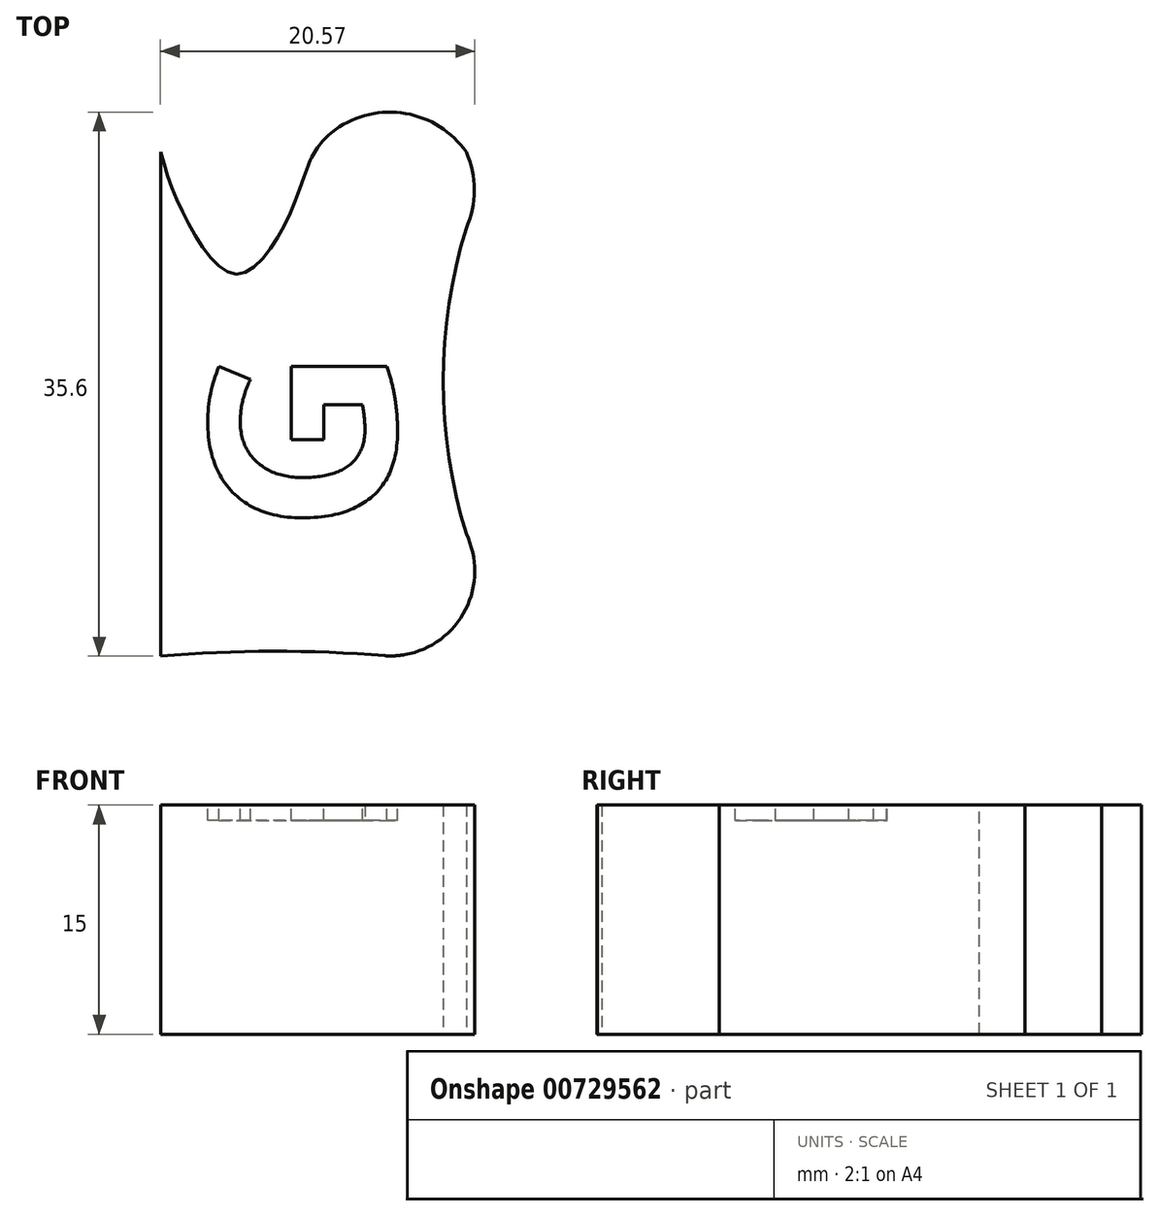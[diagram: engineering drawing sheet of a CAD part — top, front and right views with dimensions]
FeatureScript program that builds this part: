
annotation { "Feature Type Name" : "Feature", "Feature Type Description" : "" }
export const myFeature = defineFeature(function(context is Context, id is Id, definition is map)
    precondition{}
    {
        {
            var Q0;
            Q0=qCreatedBy(makeId("Top.planeOp"),FACE);
            var sketch = newSketch(context, id + "F0", { "sketchPlane" : qUnion([Q0])});
            skLineSegment(sketch, "E0", {"start": v(-17.97, 39.65) * mm, "end": v(-17.97, 6.65) * mm});
            skLineSegment(sketch, "E1", {"start": v(-17.97, 39.65) * mm, "end": v(-7.97, 39.65) * mm, "construction": true});
            skLineSegment(sketch, "E2", {"start": v(-17.97, 6.65) * mm, "end": v(-2.97, 6.65) * mm, "construction": true});
            skLineSegment(sketch, "E3", {"start": v(-17.97, 14.65) * mm, "end": v(2.03, 14.65) * mm, "construction": true});
            skLineSegment(sketch, "E4", {"start": v(-17.97, 34.65) * mm, "end": v(2.03, 34.65) * mm, "construction": true});
            skLineSegment(sketch, "E5", {"start": v(-17.97, 31.65) * mm, "end": v(-12.97, 31.65) * mm, "construction": true});
            skLineSegment(sketch, "E6", {"start": v(0.53, 24.65) * mm, "end": v(-17.97, 24.65) * mm, "construction": true});
            skLineSegment(sketch, "E7", {"start": v(-2.97, 42.25) * mm, "end": v(-17.97, 42.25) * mm, "construction": true});
            skLineSegment(sketch, "E8", {"start": v(-7.97, 39.65) * mm, "end": v(2.03, 39.65) * mm, "construction": true});
            skArc(sketch, "E9", {"start": v(2.03, 39.65) * mm, "mid": v(-1.93, 42.16) * mm, "end": v(-6.51, 41.11) * mm});
            skArc(sketch, "E10", {"start": v(2.03, 34.65) * mm, "mid": v(2.57, 37.15) * mm, "end": v(2.03, 39.65) * mm});
            skArc(sketch, "E11", {"start": v(2.03, 34.65) * mm, "mid": v(0.53, 24.65) * mm, "end": v(2.03, 14.65) * mm});
            skArc(sketch, "E12", {"start": v(-1.98, 6.74) * mm, "mid": v(2, 9.7) * mm, "end": v(2.03, 14.65) * mm});
            skArc(sketch, "E13", {"start": v(-3.27, 6.67) * mm, "mid": v(-10.62, 6.96) * mm, "end": v(-17.97, 6.65) * mm});
            skPoint(sketch, "E14", {"position": v(-15.97, 34.65) * mm});
            skPoint(sketch, "E15", {"position": v(-9.97, 34.65) * mm});
            skFitSpline(sketch, "E16", {"points": [v(-17.97, 39.65) * mm, v(-15.97, 34.65) * mm, v(-12.97, 31.65) * mm, v(-9.97, 34.65) * mm, v(-7.97, 39.65) * mm], "startDerivative": vector(5.02, -18.93) * mm, "endDerivative": vector(7.48, 18.68) * mm});
            skArc(sketch, "E17.filletArc", {"start": v(-6.51, 41.11) * mm, "mid": v(-7.58, 40.08) * mm, "end": v(-8.3, 38.77) * mm});
            skPoint(sketch, "E18.visualSharp", {"position": v(-2.97, 6.65) * mm});
            skArc(sketch, "E18.filletArc", {"start": v(-3.27, 6.67) * mm, "mid": v(-2.62, 6.66) * mm, "end": v(-1.98, 6.74) * mm});
            skSolve(sketch);
        }
        {
            var Q0;
            Q0 = qSketchRegion(id + "F0", true);
            extrude(context, id + "F1", {"entities" : qUnion([Q0]), "depth" : 15 * mm, "offsetDistance" : 25 * mm});
        }
        {
            var Q0;
            Q0=makeQuery(id+"F1.opExtrude","CAP_FACE",FACE,{"disambiguationData":[OSD([sQuery(id+"F0.wireOp",EDGE,"E0"),sQuery(id+"F0.wireOp",EDGE,"E9"),sQuery(id+"F0.wireOp",EDGE,"E10"),sQuery(id+"F0.wireOp",EDGE,"E11"),sQuery(id+"F0.wireOp",EDGE,"E12"),sQuery(id+"F0.wireOp",EDGE,"E13"),sQuery(id+"F0.wireOp",EDGE,"E16"),sQuery(id+"F0.wireOp",EDGE,"E17.filletArc"),sQuery(id+"F0.wireOp",EDGE,"E18.filletArc")])],"isStart":false});
            var sketch = newSketch(context, id + "F2", { "sketchPlane" : qUnion([Q0])});
            skText(sketch, "E19", { "text": "G", "fontName": "OpenSans-Bold.ttf"});
            skLineSegment(sketch, "E20", {"start": v(-14.72, 20.71) * mm, "end": v(-17.97, 20.71) * mm, "construction": true});
            skPoint(sketch, "E20.endSnap0", {"position": v(-17.97, 23.15) * mm});
            skPoint(sketch, "E20.endSnap1", {"position": v(-14.72, 20.71) * mm});
            skLineSegment(sketch, "E21", {"start": v(0.53, 24.65) * mm, "end": v(-2.72, 24.65) * mm, "construction": true});
            skLineSegment(sketch, "E22", {"start": v(-2.72, 26.8) * mm, "end": v(-14.72, 14.62) * mm, "construction": true});
            skPoint(sketch, "E23", {"position": v(-8.72, 20.71) * mm});
            const initialGuessF2  = {"E19": [-0.01472, 0.01462, 1, 0, 0.01219]};
            skSetInitialGuess(sketch, initialGuessF2);
            skSolve(sketch);
        }
        {
            var Q0;
            Q0=makeQuery(id+"F2.imprint","IMPRINT",FACE,{"disambiguationData":[TD([[makeQuery(id+"F2.imprint","IMPRINT",EDGE,{"derivedFrom":sQuery(id+"F2.wireOp",EDGE,"E19.sketch_text.stroke-0")}),-1.0]])]});
            extrude(context, id + "F3", {"entities" : qUnion([Q0]), "oppositeDirection" : true, "depth" : 1 * mm, "offsetDistance" : 25 * mm});
        }
        {
            var Q0;
            Q0=qCreatedBy(makeId("Right.planeOp"),FACE);
            var Q1;
            Q1=sQuery(id+"F2.wireOp",VERTEX,"E23");
            cPlane(context, id + "F4", {"entities" : qUnion([Q0, Q1]), "cplaneType" : CPlaneType.PLANE_POINT, "offset" : 25 * mm, "width" : 150 * mm, "height" : 150 * mm});
        }
        {
            var Q0;
            Q0=qCreatedBy(id+"F4.planeOp",FACE);
            var sketch = newSketch(context, id + "F5", { "sketchPlane" : qUnion([Q0])});
            skLineSegment(sketch, "E24", {"start": v(20.71, 15) * mm, "end": v(20.71, 2.07) * mm});
            skSolve(sketch);
        }
        {
            var Q0;
            Q0=makeQuery(id+"F3.opExtrude","SWEPT_BODY",BODY,{"disambiguationData":[OSD([sQuery(id+"F2.wireOp",EDGE,"E19.sketch_text.stroke-0"),sQuery(id+"F2.wireOp",EDGE,"E19.sketch_text.stroke-1"),sQuery(id+"F2.wireOp",EDGE,"E19.sketch_text.stroke-2"),sQuery(id+"F2.wireOp",EDGE,"E19.sketch_text.stroke-3"),sQuery(id+"F2.wireOp",EDGE,"E19.sketch_text.stroke-4"),sQuery(id+"F2.wireOp",EDGE,"E19.sketch_text.stroke-5"),sQuery(id+"F2.wireOp",EDGE,"E19.sketch_text.stroke-6"),sQuery(id+"F2.wireOp",EDGE,"E19.sketch_text.stroke-7"),sQuery(id+"F2.wireOp",EDGE,"E19.sketch_text.stroke-8"),sQuery(id+"F2.wireOp",EDGE,"E19.sketch_text.stroke-9"),sQuery(id+"F2.wireOp",EDGE,"E19.sketch_text.stroke-10"),sQuery(id+"F2.wireOp",EDGE,"E19.sketch_text.stroke-11"),sQuery(id+"F2.wireOp",EDGE,"E19.sketch_text.stroke-12"),sQuery(id+"F2.wireOp",EDGE,"E19.sketch_text.stroke-13"),sQuery(id+"F2.wireOp",EDGE,"E19.sketch_text.stroke-14"),sQuery(id+"F2.wireOp",EDGE,"E19.sketch_text.stroke-15"),sQuery(id+"F2.wireOp",EDGE,"E19.sketch_text.stroke-16"),sQuery(id+"F2.wireOp",EDGE,"E19.sketch_text.stroke-17"),sQuery(id+"F2.wireOp",EDGE,"E19.sketch_text.stroke-18")])]});
            var Q1;
            Q1=sQuery(id+"F5.wireOp",EDGE,"E24");
            transform(context, id + "F6", {"entities" : qUnion([Q0]), "transformType" : TransformType.ROTATION, "transformAxis" : qUnion([Q1]), "angle" : 270 * degree, "makeCopy" : false});
        }
        {
            var Q0;
            Q0=makeQuery(id+"F3.opExtrude","SWEPT_BODY",BODY,{"disambiguationData":[OSD([sQuery(id+"F2.wireOp",EDGE,"E19.sketch_text.stroke-0"),sQuery(id+"F2.wireOp",EDGE,"E19.sketch_text.stroke-1"),sQuery(id+"F2.wireOp",EDGE,"E19.sketch_text.stroke-2"),sQuery(id+"F2.wireOp",EDGE,"E19.sketch_text.stroke-3"),sQuery(id+"F2.wireOp",EDGE,"E19.sketch_text.stroke-4"),sQuery(id+"F2.wireOp",EDGE,"E19.sketch_text.stroke-5"),sQuery(id+"F2.wireOp",EDGE,"E19.sketch_text.stroke-6"),sQuery(id+"F2.wireOp",EDGE,"E19.sketch_text.stroke-7"),sQuery(id+"F2.wireOp",EDGE,"E19.sketch_text.stroke-8"),sQuery(id+"F2.wireOp",EDGE,"E19.sketch_text.stroke-9"),sQuery(id+"F2.wireOp",EDGE,"E19.sketch_text.stroke-10"),sQuery(id+"F2.wireOp",EDGE,"E19.sketch_text.stroke-11"),sQuery(id+"F2.wireOp",EDGE,"E19.sketch_text.stroke-12"),sQuery(id+"F2.wireOp",EDGE,"E19.sketch_text.stroke-13"),sQuery(id+"F2.wireOp",EDGE,"E19.sketch_text.stroke-14"),sQuery(id+"F2.wireOp",EDGE,"E19.sketch_text.stroke-15"),sQuery(id+"F2.wireOp",EDGE,"E19.sketch_text.stroke-16"),sQuery(id+"F2.wireOp",EDGE,"E19.sketch_text.stroke-17"),sQuery(id+"F2.wireOp",EDGE,"E19.sketch_text.stroke-18")])]});
            var Q1;
            Q1=makeQuery(id+"F1.opExtrude","SWEPT_BODY",BODY,{"disambiguationData":[OSD([sQuery(id+"F0.wireOp",EDGE,"E0"),sQuery(id+"F0.wireOp",EDGE,"E9"),sQuery(id+"F0.wireOp",EDGE,"E10"),sQuery(id+"F0.wireOp",EDGE,"E11"),sQuery(id+"F0.wireOp",EDGE,"E12"),sQuery(id+"F0.wireOp",EDGE,"E13"),sQuery(id+"F0.wireOp",EDGE,"E16"),sQuery(id+"F0.wireOp",EDGE,"E17.filletArc"),sQuery(id+"F0.wireOp",EDGE,"E18.filletArc")])]});
            booleanBodies(context, id + "F7", {"operationType" : BooleanOperationType.SUBTRACTION, "tools" : qUnion([Q0]), "targets" : qUnion([Q1])});
        }
    });
